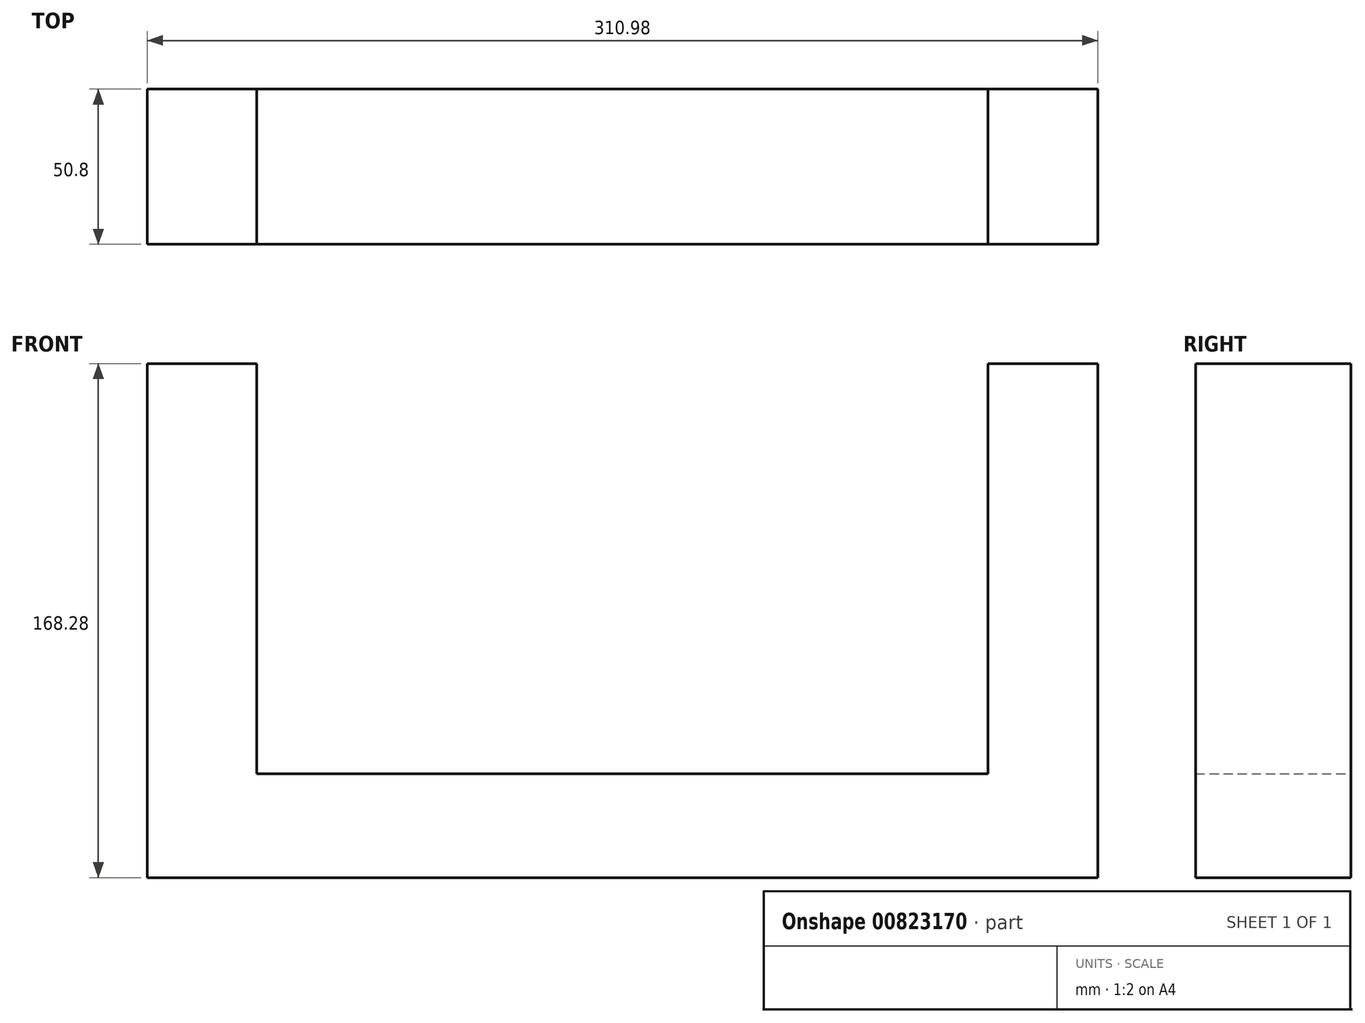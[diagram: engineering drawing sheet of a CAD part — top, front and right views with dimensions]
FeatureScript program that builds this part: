
annotation { "Feature Type Name" : "Feature", "Feature Type Description" : "" }
export const myFeature = defineFeature(function(context is Context, id is Id, definition is map)
    precondition{}
    {
        {
            var Q0;
            Q0=qCreatedBy(makeId("Front.planeOp"),FACE);
            var sketch = newSketch(context, id + "F0", { "sketchPlane" : qUnion([Q0])});
            skLineSegment(sketch, "E0", {"start": v(0, 0) * mm, "end": v(0, 134.35) * mm});
            skLineSegment(sketch, "E1", {"start": v(0, 134.35) * mm, "end": v(35.84, 134.35) * mm});
            skLineSegment(sketch, "E2", {"start": v(35.84, 134.35) * mm, "end": v(35.84, 0) * mm});
            skLineSegment(sketch, "E3", {"start": v(35.84, 0) * mm, "end": v(275.05, 0) * mm});
            skLineSegment(sketch, "E4", {"start": v(275.05, 0) * mm, "end": v(275.05, 134.35) * mm});
            skLineSegment(sketch, "E5", {"start": v(275.05, 134.35) * mm, "end": v(310.98, 134.35) * mm});
            skLineSegment(sketch, "E6", {"start": v(310.98, 134.35) * mm, "end": v(310.98, -33.93) * mm});
            skLineSegment(sketch, "E7", {"start": v(310.98, -33.93) * mm, "end": v(0, -33.93) * mm});
            skLineSegment(sketch, "E8", {"start": v(0, -33.93) * mm, "end": v(0, 0) * mm});
            skSolve(sketch);
        }
        {
            var Q0;
            Q0 = qSketchRegion(id + "F0", true);
            extrude(context, id + "F1", {"entities" : qUnion([Q0]), "depth" : 50.8 * mm, "offsetDistance" : 25.4 * mm});
        }
    });
